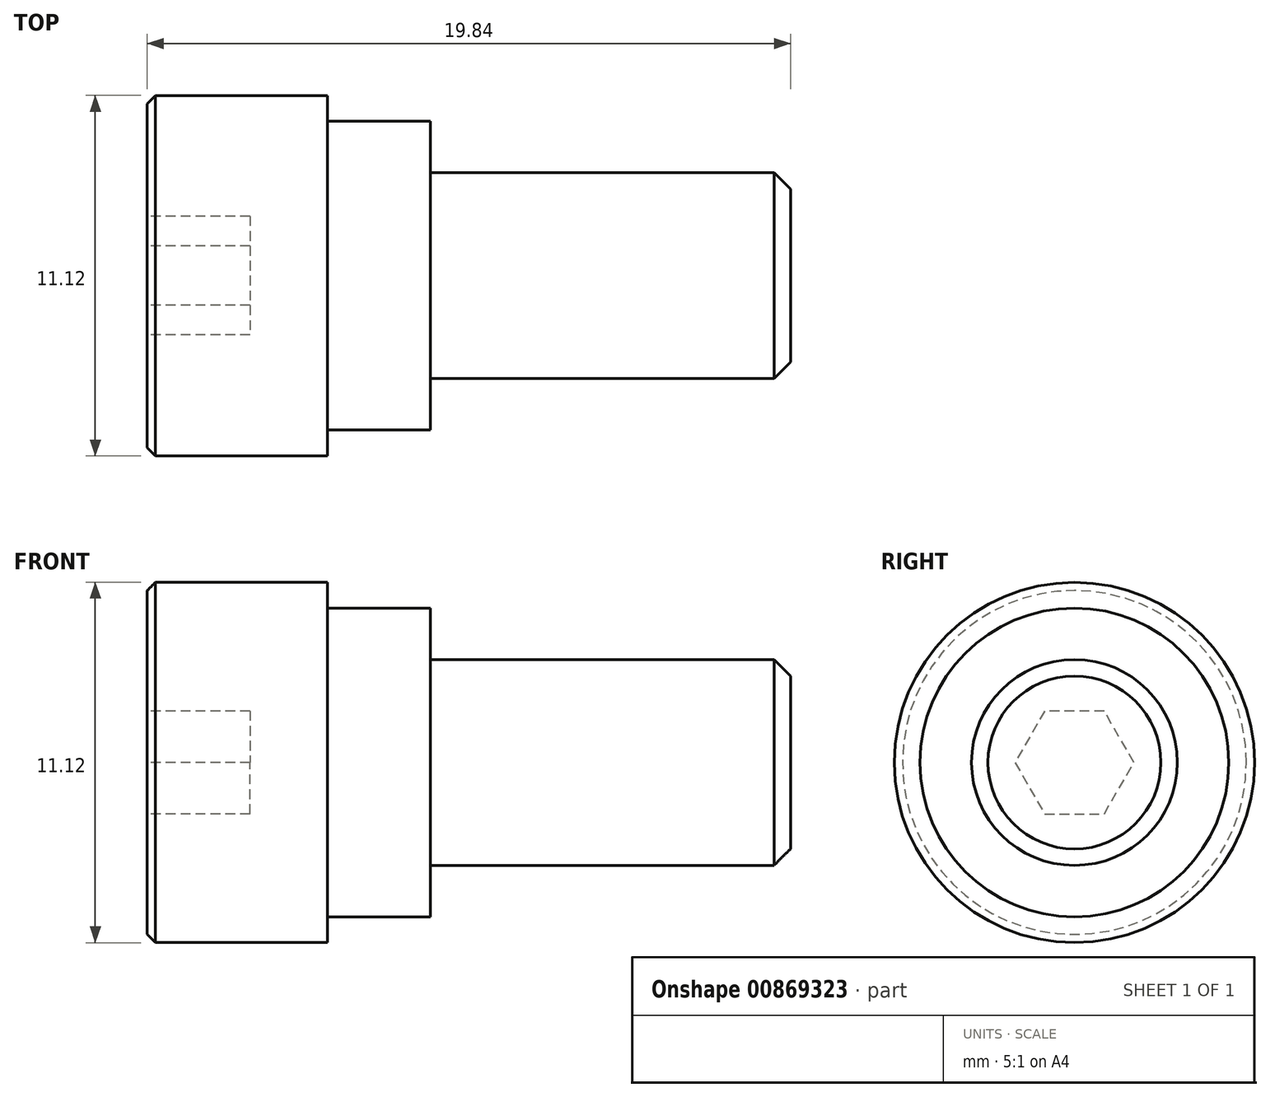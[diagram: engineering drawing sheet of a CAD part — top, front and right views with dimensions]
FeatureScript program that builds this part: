
annotation { "Feature Type Name" : "Feature", "Feature Type Description" : "" }
export const myFeature = defineFeature(function(context is Context, id is Id, definition is map)
    precondition{}
    {
        {
            var Q0;
            Q0=qCreatedBy(makeId("Front.planeOp"),FACE);
            var sketch = newSketch(context, id + "F0", { "sketchPlane" : qUnion([Q0])});
            skLineSegment(sketch, "E0.bottom", {"start": v(1.59, 4.76) * mm, "end": v(-1.59, 4.76) * mm});
            skLineSegment(sketch, "E0.top", {"start": v(1.59, -4.76) * mm, "end": v(-1.59, -4.76) * mm});
            skLineSegment(sketch, "E0.left", {"start": v(1.59, 4.76) * mm, "end": v(1.59, -4.76) * mm});
            skLineSegment(sketch, "E0.right", {"start": v(-1.59, 4.76) * mm, "end": v(-1.59, -4.76) * mm});
            skPoint(sketch, "E0.middle", {"position": v(0, 0) * mm});
            skLineSegment(sketch, "E1.bottom", {"start": v(-7.14, -5.56) * mm, "end": v(-1.59, -5.56) * mm});
            skLineSegment(sketch, "E1.top", {"start": v(-7.14, 5.56) * mm, "end": v(-1.59, 5.56) * mm});
            skLineSegment(sketch, "E1.left", {"start": v(-7.14, -5.56) * mm, "end": v(-7.14, 5.56) * mm});
            skLineSegment(sketch, "E1.right", {"start": v(-1.59, -5.56) * mm, "end": v(-1.59, 5.56) * mm});
            skLineSegment(sketch, "E2.bottom", {"start": v(1.59, 3.17) * mm, "end": v(12.7, 3.18) * mm});
            skLineSegment(sketch, "E2.top", {"start": v(1.59, -3.18) * mm, "end": v(12.7, -3.17) * mm});
            skLineSegment(sketch, "E2.left", {"start": v(1.59, 3.17) * mm, "end": v(1.59, -3.18) * mm});
            skLineSegment(sketch, "E2.right", {"start": v(12.7, 3.18) * mm, "end": v(12.7, -3.18) * mm});
            skLineSegment(sketch, "E3", {"start": v(-7.14, 0) * mm, "end": v(12.7, 0) * mm});
            skSolve(sketch);
        }
        {
            var Q0;
            {var subQ2=sQuery(id+"F0.wireOp",EDGE,"E1.top");Q0=makeQuery(id+"F0.imprint","IMPRINT",FACE,{"disambiguationData":[TD([[makeQuery(id+"F0.imprint","IMPRINT",EDGE,{"derivedFrom":subQ2}),-1.0]])]});}
            var Q1;
            Q1=sQuery(id+"F0.wireOp",EDGE,"E3");
            revolve(context, id + "F1", {"surfaceOperationType" : NewSurfaceOperationType.NEW, "entities" : qUnion([Q0]), "axis" : qUnion([Q1]), "revolveType" : RevolveType.FULL});
        }
        {
            var Q0;
            {var subQ5=sQuery(id+"F0.wireOp",EDGE,"E0.bottom");Q0=makeQuery(id+"F0.imprint","IMPRINT",FACE,{"disambiguationData":[TD([[makeQuery(id+"F0.imprint","IMPRINT",EDGE,{"derivedFrom":subQ5}),1.0]])]});}
            var Q1;
            Q1=sQuery(id+"F0.wireOp",EDGE,"E3");
            revolve(context, id + "F2", {"operationType" : NewBodyOperationType.ADD, "surfaceOperationType" : NewSurfaceOperationType.NEW, "entities" : qUnion([Q0]), "axis" : qUnion([Q1]), "revolveType" : RevolveType.FULL});
        }
        {
            var Q0;
            {var subQ0=sQuery(id+"F0.wireOp",EDGE,"E2.bottom");Q0=makeQuery(id+"F0.imprint","IMPRINT",FACE,{"disambiguationData":[TD([[makeQuery(id+"F0.imprint","IMPRINT",EDGE,{"derivedFrom":subQ0}),-1.0]])]});}
            var Q1;
            Q1=sQuery(id+"F0.wireOp",EDGE,"E3");
            revolve(context, id + "F3", {"operationType" : NewBodyOperationType.ADD, "surfaceOperationType" : NewSurfaceOperationType.NEW, "entities" : qUnion([Q0]), "axis" : qUnion([Q1]), "revolveType" : RevolveType.FULL});
        }
        {
            var Q0;
            Q0=makeQuery(id+"F1.opRevolve","SWEPT_FACE",FACE,{"disambiguationData":[OSD([sQuery(id+"F0.wireOp",EDGE,"E1.left")])]});
            var sketch = newSketch(context, id + "F4", { "sketchPlane" : qUnion([Q0])});
            skCircle(sketch, "E4.cCircle", {"center": v(0, 0) * mm, "radius": 1.59 * mm, "construction": true});
            skLineSegment(sketch, "E4.0", {"start": v(0.92, 1.59) * mm, "end": v(1.83, 0) * mm});
            skLineSegment(sketch, "E4.1", {"start": v(1.83, 0) * mm, "end": v(0.92, -1.59) * mm});
            skLineSegment(sketch, "E4.2", {"start": v(0.92, -1.59) * mm, "end": v(-0.92, -1.59) * mm});
            skLineSegment(sketch, "E4.3", {"start": v(-0.92, -1.59) * mm, "end": v(-1.83, 0) * mm});
            skLineSegment(sketch, "E4.4", {"start": v(-1.83, 0) * mm, "end": v(-0.92, 1.59) * mm});
            skLineSegment(sketch, "E4.5", {"start": v(-0.92, 1.59) * mm, "end": v(0.92, 1.59) * mm});
            skPoint(sketch, "E4.0.midPoint", {"position": v(1.37, 0.8) * mm});
            skSolve(sketch);
        }
        {
            var Q0;
            Q0=makeQuery(id+"F4.imprint","IMPRINT",FACE,{"disambiguationData":[TD([[makeQuery(id+"F4.imprint","IMPRINT",EDGE,{"derivedFrom":sQuery(id+"F4.wireOp",EDGE,"E4.0")}),-1.0]])]});
            extrude(context, id + "F5", {"entities" : qUnion([Q0]), "operationType" : NewBodyOperationType.REMOVE, "oppositeDirection" : true, "depth" : 3.17 * mm, "offsetDistance" : 25.4 * mm});
        }
        {
            var Q0;
            Q0=makeQuery(id+"F1.opRevolve","SWEPT_EDGE",EDGE,{"disambiguationData":[OSD([sQuery(id+"F0.wireOp",EDGE,"E1.top"),sQuery(id+"F0.wireOp",EDGE,"E1.left")])]});
            chamfer(context, id + "F6", {"entities" : qUnion([Q0]), "width" : 0.25 * mm, "tangentPropagation" : true});
        }
        {
            var Q0;
            Q0=makeQuery(id+"F3.opRevolve","SWEPT_EDGE",EDGE,{"disambiguationData":[OSD([sQuery(id+"F0.wireOp",EDGE,"E2.bottom"),sQuery(id+"F0.wireOp",EDGE,"E2.right")])]});
            chamfer(context, id + "F7", {"entities" : qUnion([Q0]), "width" : 0.5 * mm, "tangentPropagation" : true});
        }
    });
